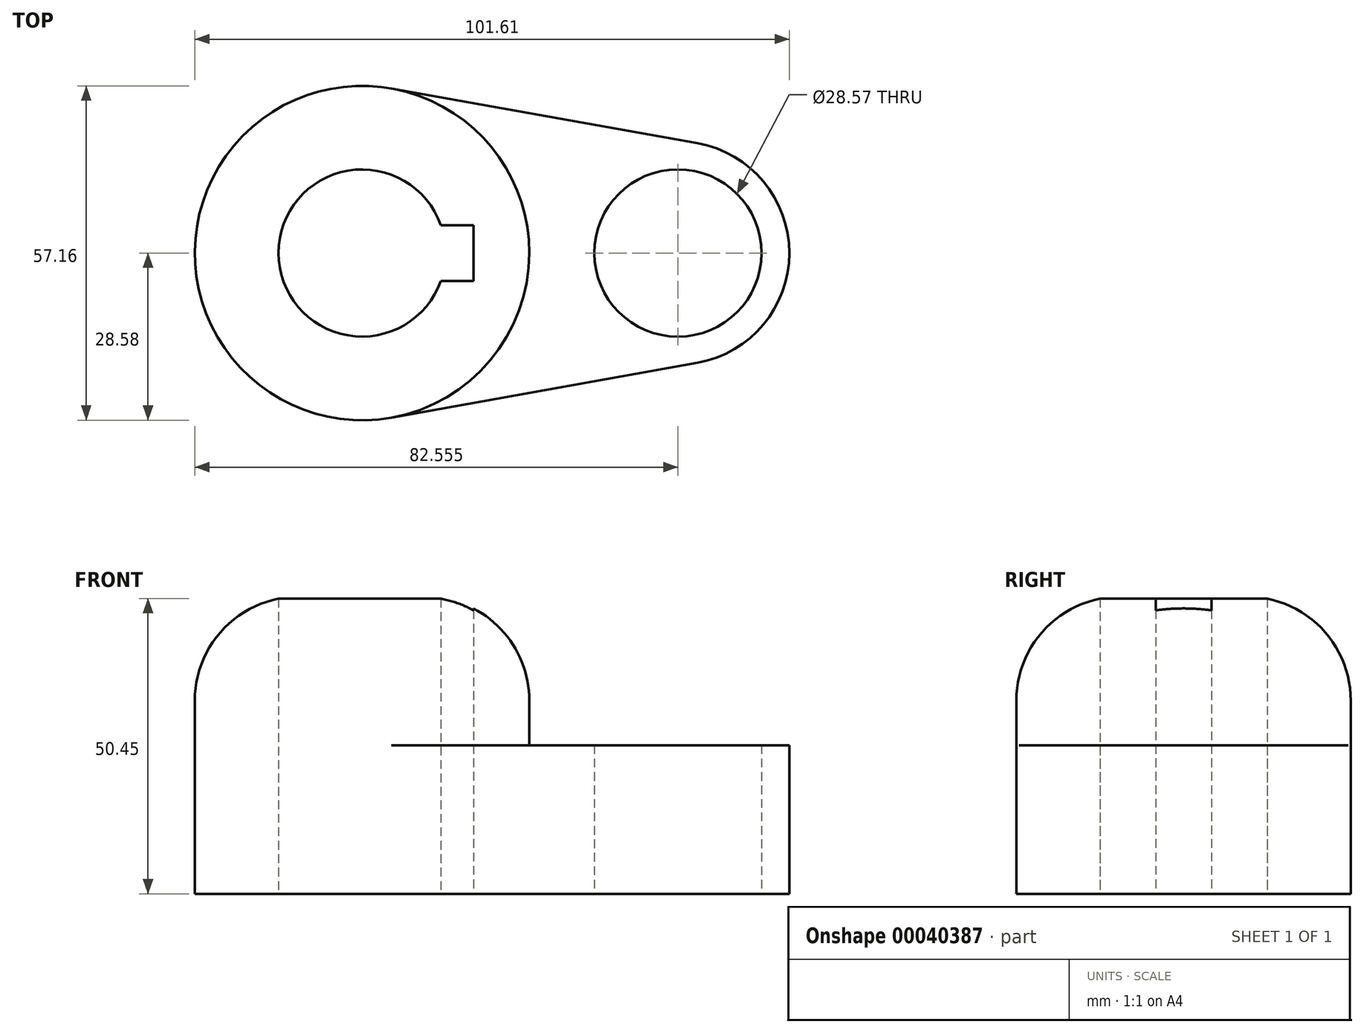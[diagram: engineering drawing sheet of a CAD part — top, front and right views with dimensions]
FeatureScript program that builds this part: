
annotation { "Feature Type Name" : "Feature", "Feature Type Description" : "" }
export const myFeature = defineFeature(function(context is Context, id is Id, definition is map)
    precondition{}
    {
        {
            var Q0;
            Q0=qCreatedBy(makeId("Top.planeOp"),FACE);
            var sketch = newSketch(context, id + "F0", { "sketchPlane" : qUnion([Q0])});
            skCircle(sketch, "E0", {"center": v(0, 0) * mm, "radius": 28.58 * mm});
            skCircle(sketch, "E1", {"center": v(53.98, 0) * mm, "radius": 19.05 * mm});
            skLineSegment(sketch, "E2", {"start": v(5.04, -28.13) * mm, "end": v(57.34, -18.75) * mm});
            skLineSegment(sketch, "E3", {"start": v(5.04, 28.13) * mm, "end": v(57.34, 18.75) * mm});
            skCircle(sketch, "E4", {"center": v(0, 0) * mm, "radius": 14.29 * mm});
            skCircle(sketch, "E5", {"center": v(53.98, 0) * mm, "radius": 14.29 * mm});
            skLineSegment(sketch, "E6.rect.bottom", {"start": v(19.05, 4.76) * mm, "end": v(-19.05, 4.76) * mm});
            skLineSegment(sketch, "E6.rect.top", {"start": v(19.05, -4.76) * mm, "end": v(-19.05, -4.76) * mm});
            skLineSegment(sketch, "E6.rect.left", {"start": v(19.05, 4.76) * mm, "end": v(19.05, -4.76) * mm});
            skLineSegment(sketch, "E6.rect.right", {"start": v(-19.05, 4.76) * mm, "end": v(-19.05, -4.76) * mm});
            skSolve(sketch);
        }
        {
            var Q0;
            {var subQ5=sQuery(id+"F0.wireOp",EDGE,"E6.rect.left");Q0=makeQuery(id+"F0.imprint","IMPRINT",FACE,{"disambiguationData":[TD([[makeQuery(id+"F0.imprint","IMPRINT",EDGE,{"derivedFrom":subQ5}),1.0]])]});}
            var Q1;
            {var subQ1=sQuery(id+"F0.wireOp",EDGE,"E2");Q1=makeQuery(id+"F0.imprint","IMPRINT",FACE,{"disambiguationData":[TD([[makeQuery(id+"F0.imprint","IMPRINT",EDGE,{"derivedFrom":subQ1}),1.0]])]});}
            var Q2;
            {var subQ0=sQuery(id+"F0.wireOp",EDGE,"E6.rect.right");Q2=makeQuery(id+"F0.imprint","IMPRINT",FACE,{"disambiguationData":[TD([[makeQuery(id+"F0.imprint","IMPRINT",EDGE,{"derivedFrom":subQ0}),1.0]])]});}
            var Q3;
            Q3=makeQuery(id+"F0.imprint","IMPRINT",FACE,{"disambiguationData":[TD([[makeQuery(id+"F0.imprint","IMPRINT",EDGE,{"derivedFrom":sQuery(id+"F0.wireOp",EDGE,"E5")}),-1.0]])]});
            extrude(context, id + "F1", {"entities" : qUnion([Q0, Q1, Q2, Q3]), "depth" : 25.4 * mm});
        }
        {
            var Q0;
            {var subQ5=sQuery(id+"F0.wireOp",EDGE,"E6.rect.left");Q0=makeQuery(id+"F0.imprint","IMPRINT",FACE,{"disambiguationData":[TD([[makeQuery(id+"F0.imprint","IMPRINT",EDGE,{"derivedFrom":subQ5}),1.0]])]});}
            var Q1;
            {var subQ0=sQuery(id+"F0.wireOp",EDGE,"E6.rect.right");Q1=makeQuery(id+"F0.imprint","IMPRINT",FACE,{"disambiguationData":[TD([[makeQuery(id+"F0.imprint","IMPRINT",EDGE,{"derivedFrom":subQ0}),1.0]])]});}
            extrude(context, id + "F2", {"entities" : qUnion([Q0, Q1]), "operationType" : NewBodyOperationType.ADD, "depth" : 50.8 * mm});
        }
        {
            var Q0;
            Q0=makeQuery(id+"F2.opExtrude","CAP_EDGE",EDGE,{"disambiguationData":[OSD([sQuery(id+"F0.wireOp",EDGE,"E0")])],"isStart":false});
            fillet(context, id + "F3", {"entities" : qUnion([Q0]), "radius" : 17.78 * mm, "tangentPropagation" : true, "allowEdgeOverflow" : false});
        }
    });
